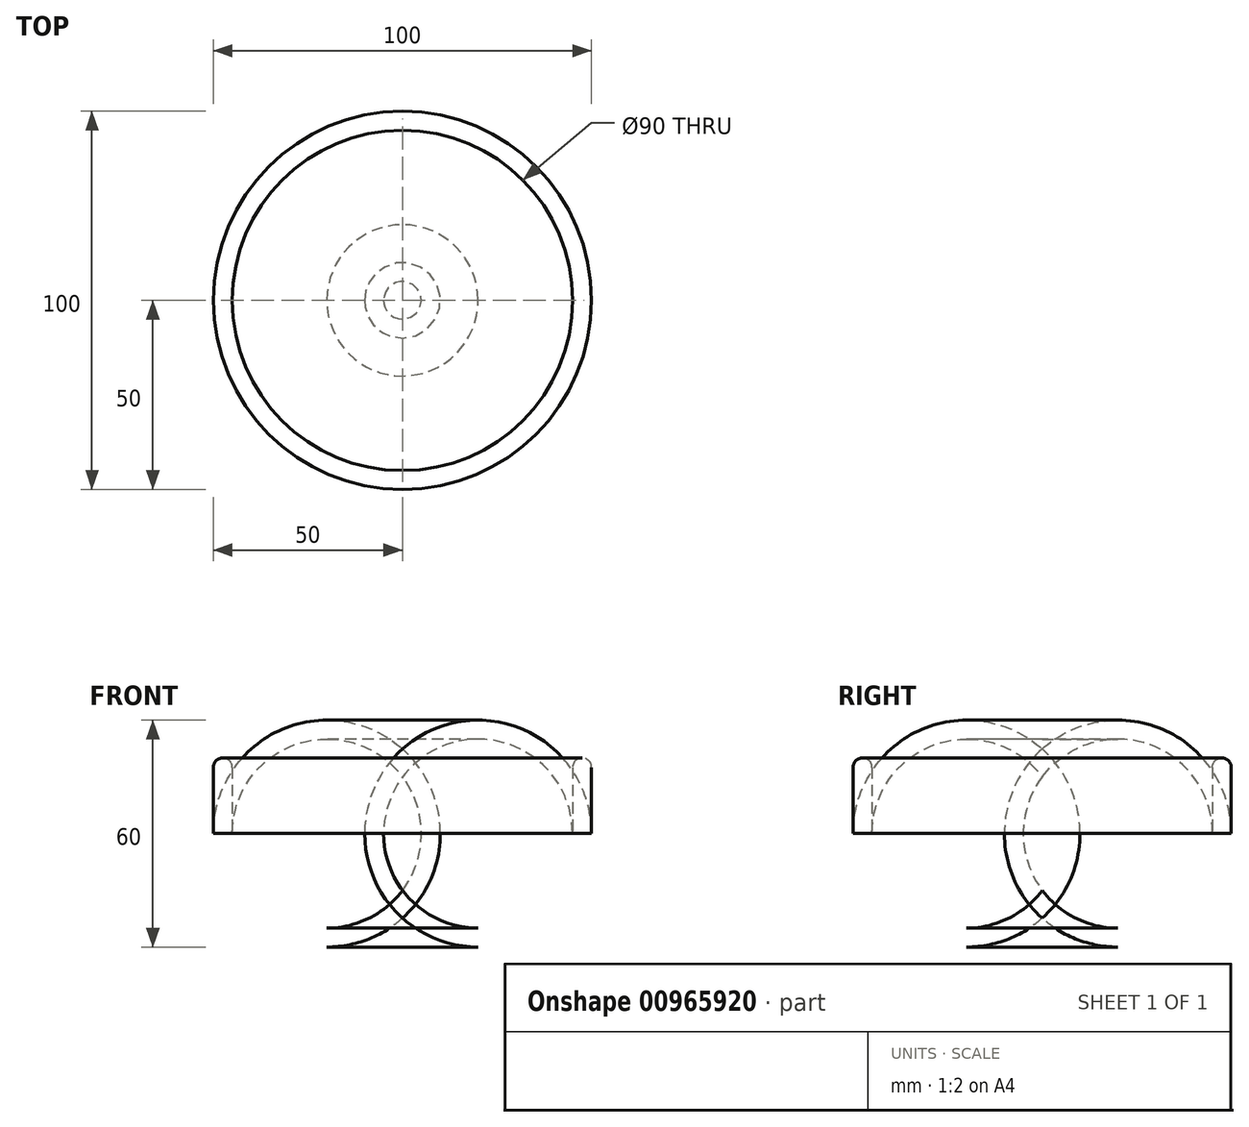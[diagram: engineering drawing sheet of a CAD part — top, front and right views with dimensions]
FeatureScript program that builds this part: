
annotation { "Feature Type Name" : "Feature", "Feature Type Description" : "" }
export const myFeature = defineFeature(function(context is Context, id is Id, definition is map)
    precondition{}
    {
        {
            var Q0;
            Q0=qCreatedBy(makeId("Top.planeOp"),FACE);
            var sketch = newSketch(context, id + "F0", { "sketchPlane" : qUnion([Q0])});
            skCircle(sketch, "E0", {"center": v(0, 0) * mm, "radius": 50 * mm});
            skSolve(sketch);
        }
        {
            var Q0;
            Q0 = qSketchRegion(id + "F0", true);
            extrude(context, id + "F1", {"entities" : qUnion([Q0]), "depth" : 50 * mm, "offsetDistance" : 25 * mm});
        }
        {
            var Q0;
            Q0=makeQuery(id+"F1.opExtrude","CAP_EDGE",EDGE,{"disambiguationData":[OSD([sQuery(id+"F0.wireOp",EDGE,"E0")])],"isStart":true});
            fillet(context, id + "F2", {"entities" : qUnion([Q0]), "radius" : 30 * mm, "tangentPropagation" : true, "allowEdgeOverflow" : false});
        }
        {
            var Q0;
            Q0=makeQuery(id+"F1.opExtrude","CAP_FACE",FACE,{"disambiguationData":[OSD([sQuery(id+"F0.wireOp",EDGE,"E0")])],"isStart":false});
            shell(context, id + "F3", {"entities" : qUnion([Q0]), "thickness" : 5 * mm});
        }
        {
            var Q0;
            {var subQ0=sQuery(id+"F0.wireOp",EDGE,"E0");Q0=makeQuery(id+"F3.opShell","OFFSET_EDGE",EDGE,{"disambiguationData":[OSD([subQ0]),TDD([makeQuery(id+"F1.opExtrude","CAP_EDGE",EDGE,{"disambiguationData":[OSD([subQ0])],"isStart":false})])]});}
            var Q1;
            Q1=makeQuery(id+"F1.opExtrude","CAP_EDGE",EDGE,{"disambiguationData":[OSD([sQuery(id+"F0.wireOp",EDGE,"E0")])],"isStart":false});
            fillet(context, id + "F4", {"entities" : qUnion([Q0, Q1]), "radius" : 2.5 * mm, "tangentPropagation" : true, "allowEdgeOverflow" : false});
        }
    });
